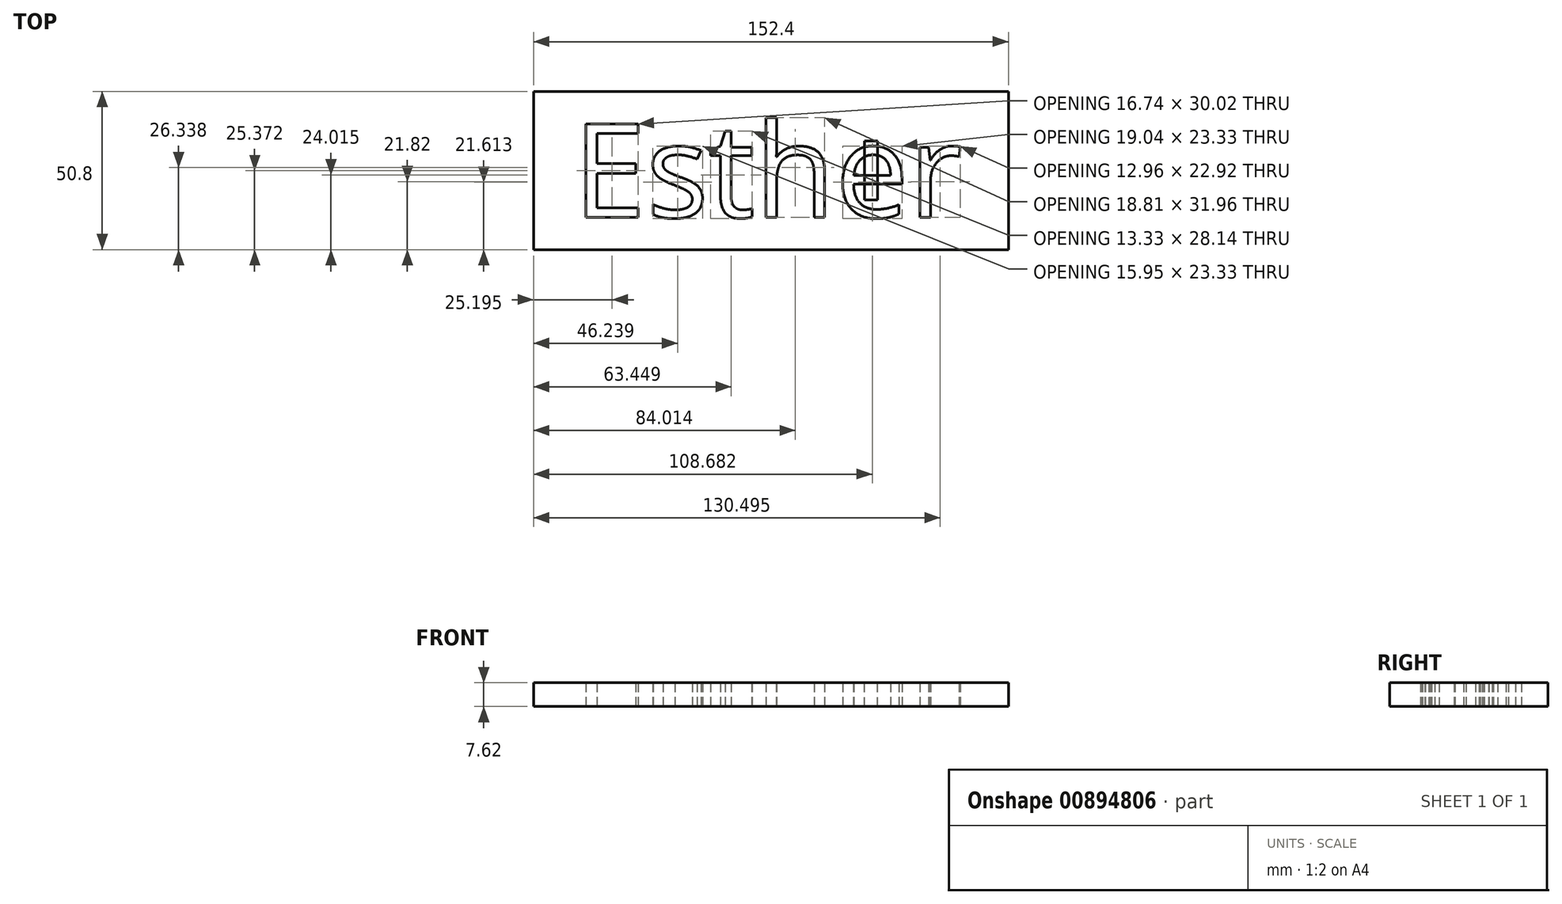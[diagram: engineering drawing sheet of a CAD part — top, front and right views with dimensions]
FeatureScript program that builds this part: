
annotation { "Feature Type Name" : "Feature", "Feature Type Description" : "" }
export const myFeature = defineFeature(function(context is Context, id is Id, definition is map)
    precondition{}
    {
        {
            var Q0;
            Q0=qCreatedBy(makeId("Top.planeOp"),FACE);
            var sketch = newSketch(context, id + "F0", { "sketchPlane" : qUnion([Q0])});
            skLineSegment(sketch, "E0.bottom", {"start": v(76.2, -25.4) * mm, "end": v(-76.2, -25.4) * mm});
            skLineSegment(sketch, "E0.top", {"start": v(76.2, 25.4) * mm, "end": v(-76.2, 25.4) * mm});
            skLineSegment(sketch, "E0.left", {"start": v(76.2, -25.4) * mm, "end": v(76.2, 25.4) * mm});
            skLineSegment(sketch, "E0.right", {"start": v(-76.2, -25.4) * mm, "end": v(-76.2, 25.4) * mm});
            skPoint(sketch, "E0.middle", {"position": v(0, 0) * mm});
            skSolve(sketch);
        }
        {
            var Q0;
            Q0=makeQuery(id+"F0.imprint","IMPRINT",FACE,{"disambiguationData":[TD([[makeQuery(id+"F0.imprint","IMPRINT",EDGE,{"derivedFrom":sQuery(id+"F0.wireOp",EDGE,"E0.bottom")}),-1.0]])]});
            extrude(context, id + "F1", {"entities" : qUnion([Q0]), "depth" : 7.62 * mm, "offsetDistance" : 25.4 * mm});
        }
        {
            var Q0;
            Q0=qCreatedBy(makeId("Top.planeOp"),FACE);
            var sketch = newSketch(context, id + "F2", { "sketchPlane" : qUnion([Q0])});
            skPoint(sketch, "E1.middle", {"position": v(0, 0) * mm});
            skText(sketch, "E2", { "text": "Esther", "fontName": "OpenSans-Regular.ttf"});
            skPoint(sketch, "E3.startSnap0", {"position": v(-63.5, 0.1) * mm});
            skPoint(sketch, "E3.endSnap0", {"position": v(-63.5, 0.1) * mm});
            const initialGuessF2  = {"E2": [-0.0635, -0.01504, 1, 0, 0.03028]};
            skSetInitialGuess(sketch, initialGuessF2);
            skSolve(sketch);
        }
        {
            var Q0;
            Q0 = qSketchRegion(id + "F2", true);
            extrude(context, id + "F3", {"entities" : qUnion([Q0]), "operationType" : NewBodyOperationType.REMOVE, "depth" : 113.8 * mm, "offsetDistance" : 25.4 * mm});
        }
        {
            var Q0;
            {var subQ0=sQuery(id+"F0.wireOp",EDGE,"E0.top");var subQ1=sQuery(id+"F0.wireOp",EDGE,"E0.right");var subQ2=sQuery(id+"F0.wireOp",EDGE,"E0.bottom");var subQ3=sQuery(id+"F0.wireOp",EDGE,"E0.left");Q0=makeQuery(id+"F3.boolean.opBoolean","SPLIT",FACE,{"disambiguationData":[TD([makeQuery(id+"F1.opExtrude","SWEPT_FACE",FACE,{"disambiguationData":[OSD([subQ2])]})])],"derivedFrom":makeQuery(id+"F1.opExtrude","CAP_FACE",FACE,{"disambiguationData":[OSD([subQ2,subQ0,subQ3,subQ1])],"isStart":false})});}
            var sketch = newSketch(context, id + "F4", { "sketchPlane" : qUnion([Q0])});
            skLineSegment(sketch, "E4.bottom", {"start": v(34.25, -9.42) * mm, "end": v(29.95, -9.42) * mm});
            skLineSegment(sketch, "E4.top", {"start": v(34.25, 9.42) * mm, "end": v(29.95, 9.42) * mm});
            skLineSegment(sketch, "E4.left", {"start": v(34.25, -9.42) * mm, "end": v(34.25, 9.42) * mm});
            skLineSegment(sketch, "E4.right", {"start": v(29.95, -9.42) * mm, "end": v(29.95, 9.42) * mm});
            skPoint(sketch, "E4.middle", {"position": v(32.1, 0) * mm});
            skPoint(sketch, "E4.cornerSnap0", {"position": v(34.25, -4.4) * mm});
            skSolve(sketch);
        }
        {
            var Q0;
            {var subQ0=makeQuery(id+"F1.opExtrude","CAP_FACE",FACE,{"disambiguationData":[OSD([sQuery(id+"F0.wireOp",EDGE,"E0.bottom"),sQuery(id+"F0.wireOp",EDGE,"E0.top"),sQuery(id+"F0.wireOp",EDGE,"E0.left"),sQuery(id+"F0.wireOp",EDGE,"E0.right")])],"isStart":false});var subQ4=sQuery(id+"F4.wireOp",EDGE,"E4.left");var subQ8=makeQuery(id+"F3.boolean.opBoolean","INTERSECT",EDGE,{"derivedFrom":[subQ0,makeQuery(id+"F3.opExtrude","SWEPT_FACE",FACE,{"disambiguationData":[OSD([sQuery(id+"F2.wireOp",EDGE,"E2.sketch_text.stroke-81")])]})]});var subQ10=makeQuery(id+"F4.imprint","INTERSECT",VERTEX,{"derivedFrom":[subQ8,subQ4]});Q0=makeQuery(id+"F4.imprint","IMPRINT",FACE,{"disambiguationData":[TD([[makeQuery(id+"F4.imprint","IMPRINT",EDGE,{"disambiguationData":[TD([[subQ10,-1.0]])],"derivedFrom":subQ4}),1.0]])]});}
            var Q1;
            {var subQ1=sQuery(id+"F4.wireOp",EDGE,"E4.top");Q1=makeQuery(id+"F4.imprint","IMPRINT",FACE,{"disambiguationData":[TD([[makeQuery(id+"F4.imprint","IMPRINT",EDGE,{"derivedFrom":subQ1}),1.0]])]});}
            var Q2;
            {var subQ0=sQuery(id+"F4.wireOp",EDGE,"E4.bottom");Q2=makeQuery(id+"F4.imprint","IMPRINT",FACE,{"disambiguationData":[TD([[makeQuery(id+"F4.imprint","IMPRINT",EDGE,{"derivedFrom":subQ0}),-1.0]])]});}
            extrude(context, id + "F5", {"entities" : qUnion([Q0, Q1, Q2]), "oppositeDirection" : true, "depth" : 7.62 * mm, "offsetDistance" : 25.4 * mm});
        }
    });
